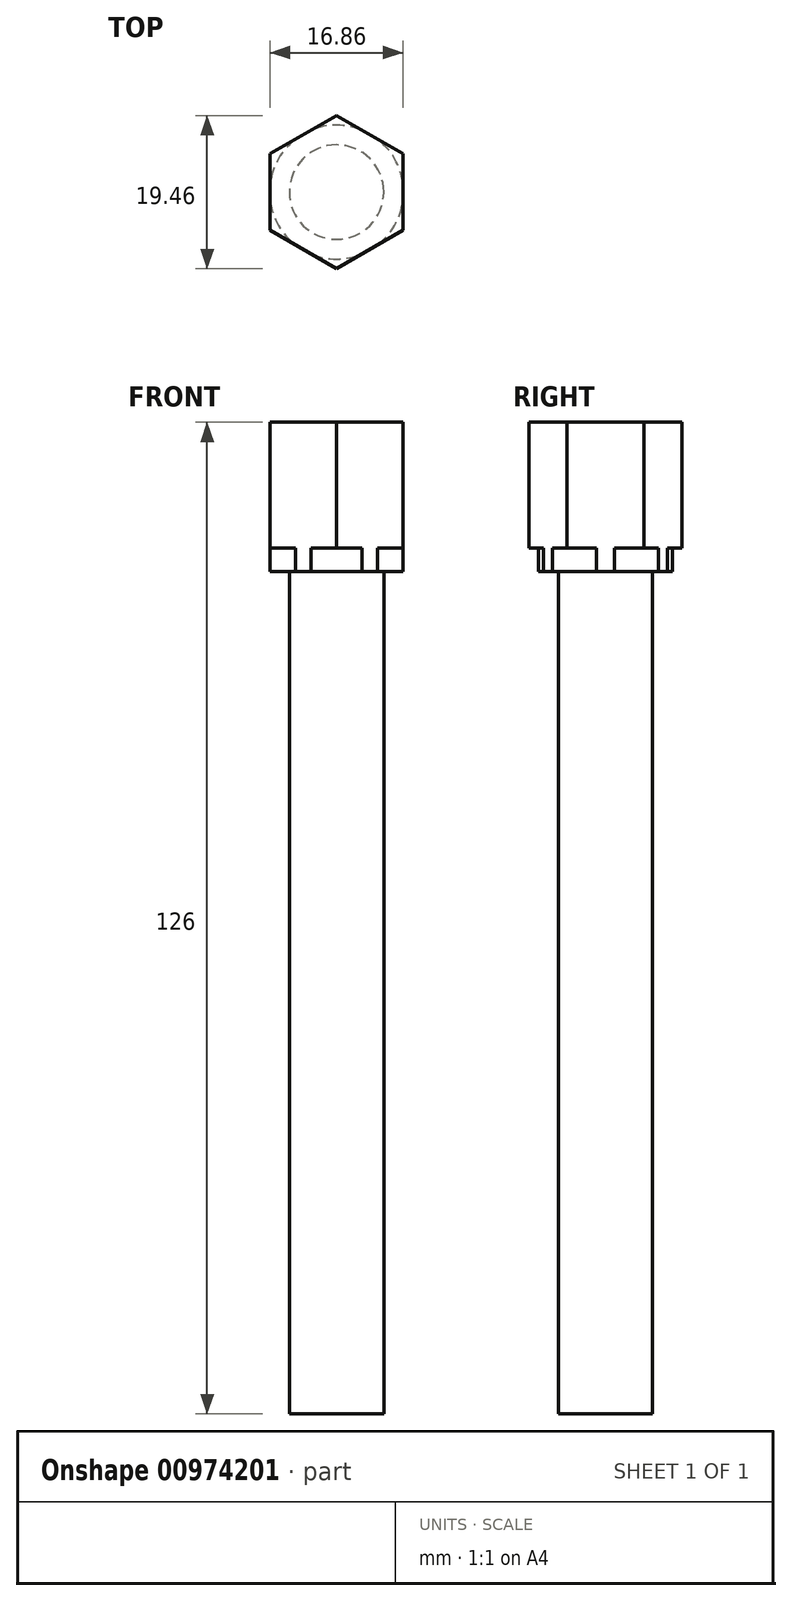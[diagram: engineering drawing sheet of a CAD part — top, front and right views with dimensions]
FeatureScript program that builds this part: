
annotation { "Feature Type Name" : "Feature", "Feature Type Description" : "" }
export const myFeature = defineFeature(function(context is Context, id is Id, definition is map)
    precondition{}
    {
        {
            var Q0;
            Q0=qCreatedBy(makeId("Top.planeOp"),FACE);
            var sketch = newSketch(context, id + "F0", { "sketchPlane" : qUnion([Q0])});
            skCircle(sketch, "E0", {"center": v(0, 0) * mm, "radius": 6 * mm});
            skCircle(sketch, "E1", {"center": v(0, 0) * mm, "radius": 8.5 * mm});
            skCircle(sketch, "E2.cCircle", {"center": v(0, 0) * mm, "radius": 8.43 * mm, "construction": true});
            skLineSegment(sketch, "E2.0", {"start": v(-8.42, 4.86) * mm, "end": v(0, 9.73) * mm});
            skLineSegment(sketch, "E2.1", {"start": v(0, 9.73) * mm, "end": v(8.42, 4.86) * mm});
            skLineSegment(sketch, "E2.2", {"start": v(8.43, 4.86) * mm, "end": v(8.42, -4.86) * mm});
            skLineSegment(sketch, "E2.3", {"start": v(8.43, -4.86) * mm, "end": v(0, -9.73) * mm});
            skLineSegment(sketch, "E2.4", {"start": v(0, -9.73) * mm, "end": v(-8.42, -4.86) * mm});
            skLineSegment(sketch, "E2.5", {"start": v(-8.43, -4.86) * mm, "end": v(-8.42, 4.86) * mm});
            skPoint(sketch, "E2.0.midPoint", {"position": v(-4.21, 7.3) * mm});
            skSolve(sketch);
        }
        {
            var Q0;
            Q0=makeQuery(id+"F0.imprint","IMPRINT",FACE,{"disambiguationData":[TD([[makeQuery(id+"F0.imprint","IMPRINT",EDGE,{"derivedFrom":sQuery(id+"F0.wireOp",EDGE,"E0")}),-1.0]])]});
            var Q1;
            {var subQ0=sQuery(id+"F0.wireOp",EDGE,"E2.0");var subQ1=sQuery(id+"F0.wireOp",EDGE,"E1");var subQ2=makeQuery(id+"F0.imprint","INTERSECT",VERTEX,{"disambiguationData":[OD(1.0)],"derivedFrom":[subQ1,subQ0]});Q1=makeQuery(id+"F0.imprint","IMPRINT",FACE,{"disambiguationData":[TD([[makeQuery(id+"F0.imprint","IMPRINT",EDGE,{"disambiguationData":[TD([[subQ2,-1.0]])],"derivedFrom":subQ1}),-1.0]])]});}
            var Q2;
            {var subQ0=sQuery(id+"F0.wireOp",EDGE,"E2.5");var subQ1=sQuery(id+"F0.wireOp",EDGE,"E1");var subQ2=makeQuery(id+"F0.imprint","INTERSECT",VERTEX,{"disambiguationData":[OD(1.0)],"derivedFrom":[subQ1,subQ0]});Q2=makeQuery(id+"F0.imprint","IMPRINT",FACE,{"disambiguationData":[TD([[makeQuery(id+"F0.imprint","IMPRINT",EDGE,{"disambiguationData":[TD([[subQ2,-1.0]])],"derivedFrom":subQ1}),-1.0]])]});}
            var Q3;
            {var subQ0=sQuery(id+"F0.wireOp",EDGE,"E2.4");var subQ1=sQuery(id+"F0.wireOp",EDGE,"E1");var subQ2=makeQuery(id+"F0.imprint","INTERSECT",VERTEX,{"disambiguationData":[OD(1.0)],"derivedFrom":[subQ1,subQ0]});Q3=makeQuery(id+"F0.imprint","IMPRINT",FACE,{"disambiguationData":[TD([[makeQuery(id+"F0.imprint","IMPRINT",EDGE,{"disambiguationData":[TD([[subQ2,-1.0]])],"derivedFrom":subQ1}),-1.0]])]});}
            var Q4;
            {var subQ0=sQuery(id+"F0.wireOp",EDGE,"E2.3");var subQ1=sQuery(id+"F0.wireOp",EDGE,"E1");var subQ2=makeQuery(id+"F0.imprint","INTERSECT",VERTEX,{"disambiguationData":[OD(1.0)],"derivedFrom":[subQ1,subQ0]});Q4=makeQuery(id+"F0.imprint","IMPRINT",FACE,{"disambiguationData":[TD([[makeQuery(id+"F0.imprint","IMPRINT",EDGE,{"disambiguationData":[TD([[subQ2,-1.0]])],"derivedFrom":subQ1}),-1.0]])]});}
            var Q5;
            {var subQ0=sQuery(id+"F0.wireOp",EDGE,"E2.1");var subQ1=sQuery(id+"F0.wireOp",EDGE,"E1");var subQ2=makeQuery(id+"F0.imprint","INTERSECT",VERTEX,{"disambiguationData":[OD(0.0)],"derivedFrom":[subQ1,subQ0]});Q5=makeQuery(id+"F0.imprint","IMPRINT",FACE,{"disambiguationData":[TD([[makeQuery(id+"F0.imprint","IMPRINT",EDGE,{"disambiguationData":[TD([[subQ2,1.0]])],"derivedFrom":subQ1}),-1.0]])]});}
            var Q6;
            {var subQ0=sQuery(id+"F0.wireOp",EDGE,"E2.1");var subQ1=sQuery(id+"F0.wireOp",EDGE,"E1");var subQ2=makeQuery(id+"F0.imprint","INTERSECT",VERTEX,{"disambiguationData":[OD(1.0)],"derivedFrom":[subQ1,subQ0]});Q6=makeQuery(id+"F0.imprint","IMPRINT",FACE,{"disambiguationData":[TD([[makeQuery(id+"F0.imprint","IMPRINT",EDGE,{"disambiguationData":[TD([[subQ2,-1.0]])],"derivedFrom":subQ1}),-1.0]])]});}
            var Q7;
            Q7=makeQuery(id+"F0.imprint","IMPRINT",FACE,{"disambiguationData":[TD([[makeQuery(id+"F0.imprint","IMPRINT",EDGE,{"derivedFrom":sQuery(id+"F0.wireOp",EDGE,"E0")}),1.0]])]});
            var Q8;
            Q8=sQuery(id+"F0.wireOp",EDGE,"E2.1");
            var Q9;
            Q9=sQuery(id+"F0.wireOp",EDGE,"E2.0");
            var Q10;
            Q10=sQuery(id+"F0.wireOp",EDGE,"E2.5");
            var Q11;
            Q11=sQuery(id+"F0.wireOp",EDGE,"E2.4");
            var Q12;
            Q12=sQuery(id+"F0.wireOp",EDGE,"E2.3");
            var Q13;
            Q13=sQuery(id+"F0.wireOp",EDGE,"E2.2");
            extrude(context, id + "F1", {"entities" : qUnion([Q0, Q1, Q2, Q3, Q4, Q5, Q6, Q7]), "surfaceEntities" : qUnion([Q8, Q9, Q10, Q11, Q12, Q13]), "depth" : 16 * mm, "offsetDistance" : 25 * mm});
        }
        {
            var Q0;
            Q0=makeQuery(id+"F0.imprint","IMPRINT",FACE,{"disambiguationData":[TD([[makeQuery(id+"F0.imprint","IMPRINT",EDGE,{"derivedFrom":sQuery(id+"F0.wireOp",EDGE,"E0")}),-1.0]])]});
            var Q1;
            Q1=makeQuery(id+"F0.imprint","IMPRINT",FACE,{"disambiguationData":[TD([[makeQuery(id+"F0.imprint","IMPRINT",EDGE,{"derivedFrom":sQuery(id+"F0.wireOp",EDGE,"E0")}),1.0]])]});
            extrude(context, id + "F2", {"entities" : qUnion([Q0, Q1]), "operationType" : NewBodyOperationType.ADD, "oppositeDirection" : true, "depth" : 3 * mm, "offsetDistance" : 25 * mm});
        }
        {
            var Q0;
            Q0=makeQuery(id+"F0.imprint","IMPRINT",FACE,{"disambiguationData":[TD([[makeQuery(id+"F0.imprint","IMPRINT",EDGE,{"derivedFrom":sQuery(id+"F0.wireOp",EDGE,"E0")}),1.0]])]});
            extrude(context, id + "F3", {"entities" : qUnion([Q0]), "operationType" : NewBodyOperationType.ADD, "flatOperationType" : FlatOperationType.REMOVE, "oppositeDirection" : true, "depth" : 110 * mm, "offsetDistance" : 25 * mm, "domain" : OperationDomain.MODEL});
        }
    });
